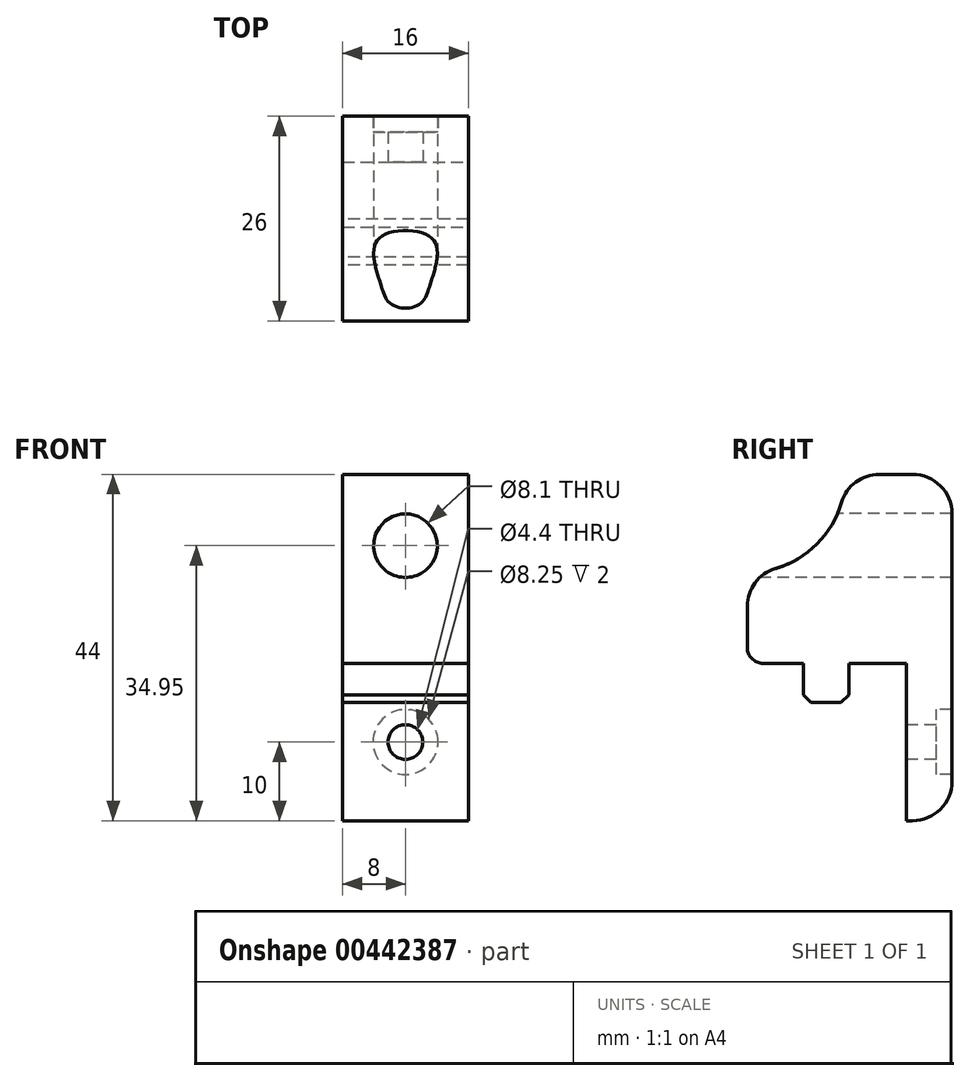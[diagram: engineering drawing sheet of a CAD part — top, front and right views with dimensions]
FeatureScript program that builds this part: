
annotation { "Feature Type Name" : "Feature", "Feature Type Description" : "" }
export const myFeature = defineFeature(function(context is Context, id is Id, definition is map)
    precondition{}
    {
        {
            var Q0;
            Q0=qCreatedBy(makeId("Front.planeOp"),FACE);
            var sketch = newSketch(context, id + "F0", { "sketchPlane" : qUnion([Q0])});
            skLineSegment(sketch, "E0.bottom", {"start": v(8, -12) * mm, "end": v(-8, -12) * mm});
            skLineSegment(sketch, "E0.top", {"start": v(8, 12) * mm, "end": v(-8, 12) * mm});
            skLineSegment(sketch, "E0.left", {"start": v(8, -12) * mm, "end": v(8, 12) * mm});
            skLineSegment(sketch, "E0.right", {"start": v(-8, -12) * mm, "end": v(-8, 12) * mm});
            skPoint(sketch, "E0.middle", {"position": v(0, 0) * mm});
            skSolve(sketch);
        }
        {
            var Q0;
            Q0=qSketchRegion(id+"F0",true);
            extrude(context, id + "F1", {"entities" : qUnion([Q0]), "depth" : 26 * mm, "offsetDistance" : 25 * mm, "symmetric" : true});
        }
        {
            var Q0;
            Q0=makeQuery(id+"F1.opExtrude","SWEPT_FACE",FACE,{"disambiguationData":[OSD([sQuery(id+"F0.wireOp",EDGE,"E0.bottom")])]});
            var sketch = newSketch(context, id + "F2", { "sketchPlane" : qUnion([Q0])});
            skLineSegment(sketch, "E1.bottom", {"start": v(8, 0.1) * mm, "end": v(-8, 0.1) * mm});
            skLineSegment(sketch, "E1.top", {"start": v(8, 5.9) * mm, "end": v(-8, 5.9) * mm});
            skLineSegment(sketch, "E1.left", {"start": v(8, 0.1) * mm, "end": v(8, 5.9) * mm});
            skLineSegment(sketch, "E1.right", {"start": v(-8, 0.1) * mm, "end": v(-8, 5.9) * mm});
            skPoint(sketch, "E1.middle", {"position": v(0, 3) * mm});
            skLineSegment(sketch, "E2.bottom", {"start": v(-8, -13) * mm, "end": v(8, -13) * mm});
            skLineSegment(sketch, "E2.top", {"start": v(-8, -7.2) * mm, "end": v(8, -7.2) * mm});
            skLineSegment(sketch, "E2.left", {"start": v(-8, -13) * mm, "end": v(-8, -7.2) * mm});
            skLineSegment(sketch, "E2.right", {"start": v(8, -13) * mm, "end": v(8, -7.2) * mm});
            skSolve(sketch);
        }
        {
            var Q0;
            Q0=makeQuery(id+"F2.imprint","IMPRINT",FACE,{"disambiguationData":[TD([[makeQuery(id+"F2.imprint","IMPRINT",EDGE,{"derivedFrom":sQuery(id+"F2.wireOp",EDGE,"E1.bottom")}),-1.0]])]});
            extrude(context, id + "F3", {"entities" : qUnion([Q0]), "operationType" : NewBodyOperationType.ADD, "depth" : 5 * mm, "offsetDistance" : 25 * mm});
        }
        {
            var Q0;
            Q0=makeQuery(id+"F2.imprint","IMPRINT",FACE,{"disambiguationData":[TD([[makeQuery(id+"F2.imprint","IMPRINT",EDGE,{"derivedFrom":sQuery(id+"F2.wireOp",EDGE,"E2.bottom")}),-1.0]])]});
            extrude(context, id + "F4", {"entities" : qUnion([Q0]), "operationType" : NewBodyOperationType.ADD, "depth" : 20 * mm, "offsetDistance" : 25 * mm});
        }
        {
            var Q0;
            Q0=makeQuery(id+"F1.opExtrude","CAP_FACE",FACE,{"disambiguationData":[OSD([sQuery(id+"F0.wireOp",EDGE,"E0.bottom"),sQuery(id+"F0.wireOp",EDGE,"E0.top"),sQuery(id+"F0.wireOp",EDGE,"E0.left"),sQuery(id+"F0.wireOp",EDGE,"E0.right")])],"isStart":false});
            var sketch = newSketch(context, id + "F5", { "sketchPlane" : qUnion([Q0])});
            skCircle(sketch, "E3", {"center": v(0, 2.95) * mm, "radius": 4.05 * mm});
            skSolve(sketch);
        }
        {
            var Q0;
            Q0=qSketchRegion(id+"F5",true);
            extrude(context, id + "F6", {"entities" : qUnion([Q0]), "operationType" : NewBodyOperationType.REMOVE, "endBound" : BoundingType.THROUGH_ALL, "oppositeDirection" : true, "depth" : 30 * mm, "offsetDistance" : 25 * mm});
        }
        {
            var Q0;
            Q0=makeQuery(id+"F4.boolean.opBoolean","MERGE",FACE,{"derivedFrom":[makeQuery(id+"F1.opExtrude","CAP_FACE",FACE,{"disambiguationData":[OSD([sQuery(id+"F0.wireOp",EDGE,"E0.bottom"),sQuery(id+"F0.wireOp",EDGE,"E0.top"),sQuery(id+"F0.wireOp",EDGE,"E0.left"),sQuery(id+"F0.wireOp",EDGE,"E0.right")])],"isStart":true}),makeQuery(id+"F4.opExtrude","SWEPT_FACE",FACE,{"disambiguationData":[OSD([sQuery(id+"F2.wireOp",EDGE,"E2.bottom")])]})]});
            var sketch = newSketch(context, id + "F7", { "sketchPlane" : qUnion([Q0])});
            skLineSegment(sketch, "E4", {"start": v(-8, -22) * mm, "end": v(8, -22) * mm, "construction": true});
            skPoint(sketch, "E5", {"position": v(0, -22) * mm});
            skSolve(sketch);
        }
        {
            var Q0;
            Q0=sQuery(id+"F7.wireOp",VERTEX,"E5");
            var Q1;
            Q1=sQuery(id+"F7.wireOp",VERTEX,"7c64e804-d5a0-4580-aa40-0e1040ca2d0c0.MirrorP");
            var Q2;
            Q2=makeQuery(id+"F1.opExtrude","SWEPT_BODY",BODY,{"disambiguationData":[OSD([sQuery(id+"F0.wireOp",EDGE,"E0.bottom"),sQuery(id+"F0.wireOp",EDGE,"E0.top"),sQuery(id+"F0.wireOp",EDGE,"E0.left"),sQuery(id+"F0.wireOp",EDGE,"E0.right")])]});
            hole(context, id + "F8", {"style" : HoleStyle.C_BORE, "endStyle" : HoleEndStyle.THROUGH, "holeDiameter" : 4.4 * mm, "cBoreDiameter" : 8.25 * mm, "cBoreDepth" : 2 * mm, "majorDiameter" : 5 * mm, "isTappedThrough" : true, "tappedDepth" : 12 * mm, "tapClearance" : 3, "locations" : qUnion([Q0, Q1]), "scope" : qUnion([Q2])});
        }
        {
            var Q0;
            Q0=makeQuery(id+"F3.opExtrude","CAP_EDGE",EDGE,{"disambiguationData":[OSD([sQuery(id+"F2.wireOp",EDGE,"E1.top")])],"isStart":false});
            var Q1;
            Q1=makeQuery(id+"F3.opExtrude","CAP_EDGE",EDGE,{"disambiguationData":[OSD([sQuery(id+"F2.wireOp",EDGE,"E1.bottom")])],"isStart":false});
            chamfer(context, id + "F9", {"entities" : qUnion([Q0, Q1]), "width" : 1 * mm, "tangentPropagation" : true});
        }
        {
            var Q0;
            Q0=makeQuery(id+"F4.boolean.opBoolean","MERGE",FACE,{"derivedFrom":[makeQuery(id+"F3.boolean.opBoolean","MERGE",FACE,{"derivedFrom":[makeQuery(id+"F1.opExtrude","SWEPT_FACE",FACE,{"disambiguationData":[OSD([sQuery(id+"F0.wireOp",EDGE,"E0.left")])]}),makeQuery(id+"F3.opExtrude","SWEPT_FACE",FACE,{"disambiguationData":[OSD([sQuery(id+"F2.wireOp",EDGE,"E1.left")])]})]}),makeQuery(id+"F4.opExtrude","SWEPT_FACE",FACE,{"disambiguationData":[OSD([sQuery(id+"F2.wireOp",EDGE,"E2.right")])]})]});
            var sketch = newSketch(context, id + "F10", { "sketchPlane" : qUnion([Q0])});
            skCircle(sketch, "E6", {"center": v(-13, 12) * mm, "radius": 12.5 * mm});
            skSolve(sketch);
        }
        {
            var Q0;
            {var subQ0=sQuery(id+"F10.wireOp",EDGE,"E6");var subQ1=sQuery(id+"F0.wireOp",EDGE,"E0.left");var subQ2=makeQuery(id+"F1.opExtrude","SWEPT_EDGE",EDGE,{"disambiguationData":[OSD([sQuery(id+"F0.wireOp",EDGE,"E0.top"),subQ1])]});var subQ3=makeQuery(id+"F10.imprint","INTERSECT",VERTEX,{"derivedFrom":[subQ2,subQ0]});Q0=makeQuery(id+"F10.imprint","IMPRINT",FACE,{"disambiguationData":[TD([[makeQuery(id+"F10.imprint","IMPRINT",EDGE,{"disambiguationData":[TD([[subQ3,-1.0]])],"derivedFrom":subQ0}),1.0]])]});}
            var Q1;
            {var subQ0=sQuery(id+"F10.wireOp",EDGE,"E6");var subQ1=sQuery(id+"F0.wireOp",EDGE,"E0.left");var subQ4=makeQuery(id+"F1.opExtrude","CAP_EDGE",EDGE,{"disambiguationData":[OSD([subQ1])],"isStart":false});var subQ5=makeQuery(id+"F10.imprint","INTERSECT",VERTEX,{"derivedFrom":[subQ4,subQ0]});Q1=makeQuery(id+"F10.imprint","IMPRINT",FACE,{"disambiguationData":[TD([[makeQuery(id+"F10.imprint","IMPRINT",EDGE,{"disambiguationData":[TD([[subQ5,-1.0]])],"derivedFrom":subQ0}),1.0]])]});}
            extrude(context, id + "F11", {"entities" : qUnion([Q0, Q1]), "operationType" : NewBodyOperationType.REMOVE, "endBound" : BoundingType.THROUGH_ALL, "oppositeDirection" : true, "depth" : 25 * mm, "offsetDistance" : 25 * mm});
        }
        {
            var Q0;
            {var subQ0=sQuery(id+"F2.wireOp",EDGE,"E2.bottom");var subQ1=sQuery(id+"F0.wireOp",EDGE,"E0.left");var subQ2=sQuery(id+"F2.wireOp",EDGE,"E2.right");var subQ3=sQuery(id+"F10.wireOp",EDGE,"E6");Q0=makeQuery(id+"F11.boolean.opBoolean","COPY",EDGE,{"disambiguationData":[TD([makeQuery(id+"F1.opExtrude","SWEPT_FACE",FACE,{"disambiguationData":[OSD([subQ1])]})])],"derivedFrom":makeQuery(id+"F11.opExtrude","SWEPT_EDGE",EDGE,{"disambiguationData":[OSD([subQ1,subQ0,subQ2,subQ3])]})});}
            var Q1;
            {var subQ0=sQuery(id+"F2.wireOp",EDGE,"E2.bottom");var subQ1=sQuery(id+"F0.wireOp",EDGE,"E0.right");var subQ2=sQuery(id+"F0.wireOp",EDGE,"E0.left");var subQ3=sQuery(id+"F10.wireOp",EDGE,"E6");Q1=makeQuery(id+"F11.boolean.opBoolean","COPY",EDGE,{"disambiguationData":[TD([makeQuery(id+"F1.opExtrude","SWEPT_FACE",FACE,{"disambiguationData":[OSD([subQ1])]})])],"derivedFrom":makeQuery(id+"F11.opExtrude","SWEPT_EDGE",EDGE,{"disambiguationData":[OSD([subQ2,subQ0,sQuery(id+"F2.wireOp",EDGE,"E2.right"),subQ3])]})});}
            var Q2;
            Q2=makeQuery(id+"F11.boolean.opBoolean","COPY",EDGE,{"derivedFrom":makeQuery(id+"F11.opExtrude","SWEPT_EDGE",EDGE,{"disambiguationData":[OSD([sQuery(id+"F0.wireOp",EDGE,"E0.top"),sQuery(id+"F0.wireOp",EDGE,"E0.left"),sQuery(id+"F10.wireOp",EDGE,"E6")])]})});
            var Q3;
            Q3=makeQuery(id+"F1.opExtrude","CAP_EDGE",EDGE,{"disambiguationData":[OSD([sQuery(id+"F0.wireOp",EDGE,"E0.top")])],"isStart":false});
            var Q4;
            Q4=makeQuery(id+"F4.opExtrude","CAP_EDGE",EDGE,{"disambiguationData":[OSD([sQuery(id+"F2.wireOp",EDGE,"E2.bottom")])],"isStart":false});
            var Q5;
            Q5=makeQuery(id+"F1.opExtrude","CAP_EDGE",EDGE,{"disambiguationData":[OSD([sQuery(id+"F0.wireOp",EDGE,"E0.top")])],"isStart":true});
            var Q6;
            Q6=makeQuery(id+"F11.boolean.opBoolean","INTERSECT",EDGE,{"disambiguationData":[OD(0.0)],"derivedFrom":[makeQuery(id+"F1.opExtrude","CAP_FACE",FACE,{"disambiguationData":[OSD([sQuery(id+"F0.wireOp",EDGE,"E0.bottom"),sQuery(id+"F0.wireOp",EDGE,"E0.top"),sQuery(id+"F0.wireOp",EDGE,"E0.left"),sQuery(id+"F0.wireOp",EDGE,"E0.right")])],"isStart":false}),makeQuery(id+"F11.opExtrude","SWEPT_FACE",FACE,{"disambiguationData":[OSD([sQuery(id+"F10.wireOp",EDGE,"E6")])]})]});
            var Q7;
            Q7=makeQuery(id+"F11.boolean.opBoolean","INTERSECT",EDGE,{"derivedFrom":[makeQuery(id+"F1.opExtrude","SWEPT_FACE",FACE,{"disambiguationData":[OSD([sQuery(id+"F0.wireOp",EDGE,"E0.top")])]}),makeQuery(id+"F11.opExtrude","SWEPT_FACE",FACE,{"disambiguationData":[OSD([sQuery(id+"F10.wireOp",EDGE,"E6")])]})]});
            var Q8;
            Q8=makeQuery(id+"F11.boolean.opBoolean","INTERSECT",EDGE,{"disambiguationData":[OD(1.0)],"derivedFrom":[makeQuery(id+"F1.opExtrude","CAP_FACE",FACE,{"disambiguationData":[OSD([sQuery(id+"F0.wireOp",EDGE,"E0.bottom"),sQuery(id+"F0.wireOp",EDGE,"E0.top"),sQuery(id+"F0.wireOp",EDGE,"E0.left"),sQuery(id+"F0.wireOp",EDGE,"E0.right")])],"isStart":false}),makeQuery(id+"F11.opExtrude","SWEPT_FACE",FACE,{"disambiguationData":[OSD([sQuery(id+"F10.wireOp",EDGE,"E6")])]})]});
            fillet(context, id + "F12", {"entities" : qUnion([Q0, Q1, Q2, Q3, Q4, Q5, Q6, Q7, Q8]), "radius" : 5 * mm, "tangentPropagation" : true, "allowEdgeOverflow" : false});
        }
        {
            var Q0;
            Q0=makeQuery(id+"F1.opExtrude","CAP_EDGE",EDGE,{"disambiguationData":[OSD([sQuery(id+"F0.wireOp",EDGE,"E0.bottom")])],"isStart":false});
            fillet(context, id + "F13", {"entities" : qUnion([Q0]), "radius" : 2 * mm, "tangentPropagation" : true, "allowEdgeOverflow" : false});
        }
    });
